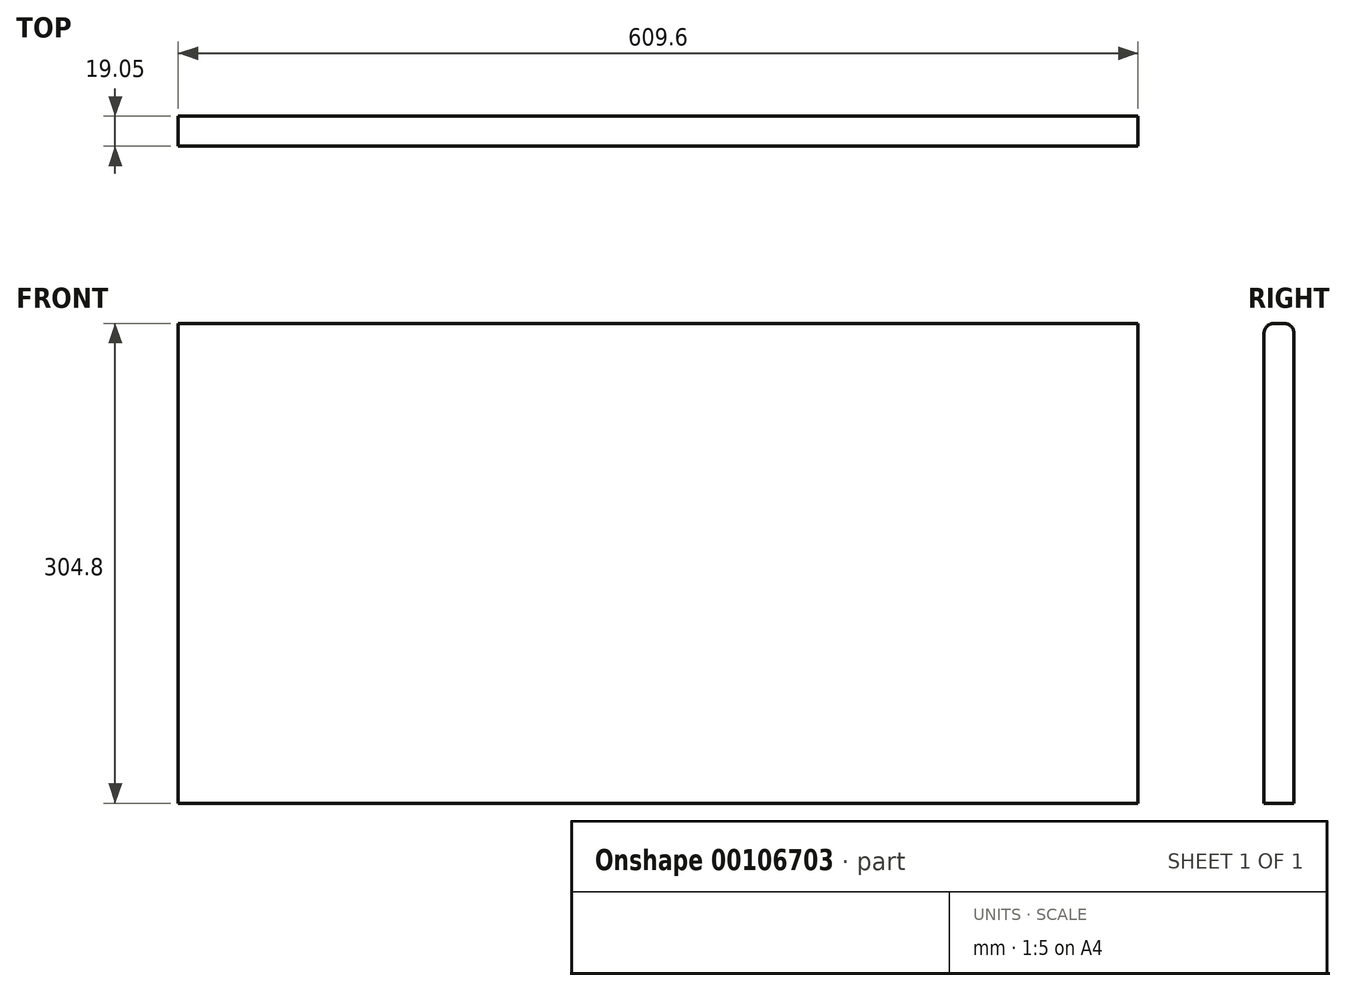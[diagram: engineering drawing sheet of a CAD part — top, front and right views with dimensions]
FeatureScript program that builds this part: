
annotation { "Feature Type Name" : "Feature", "Feature Type Description" : "" }
export const myFeature = defineFeature(function(context is Context, id is Id, definition is map)
    precondition{}
    {
        {
            var Q0;
            Q0=qCreatedBy(makeId("Front.planeOp"),FACE);
            var sketch = newSketch(context, id + "F0", { "sketchPlane" : qUnion([Q0])});
            skLineSegment(sketch, "E0.bottom", {"start": v(0, 0) * mm, "end": v(609.6, 0) * mm});
            skLineSegment(sketch, "E0.top", {"start": v(0, 304.8) * mm, "end": v(609.6, 304.8) * mm});
            skLineSegment(sketch, "E0.left", {"start": v(0, 0) * mm, "end": v(0, 304.8) * mm});
            skLineSegment(sketch, "E0.right", {"start": v(609.6, 0) * mm, "end": v(609.6, 304.8) * mm});
            skSolve(sketch);
        }
        {
            var Q0;
            Q0=makeQuery(id+"F0.imprint","IMPRINT",FACE,{"disambiguationData":[TD([[makeQuery(id+"F0.imprint","IMPRINT",EDGE,{"derivedFrom":sQuery(id+"F0.wireOp",EDGE,"E0.bottom")}),1.0]])]});
            extrude(context, id + "F1", {"entities" : qUnion([Q0]), "depth" : 19.05 * mm});
        }
        {
            var Q0;
            Q0=makeQuery(id+"F1.opExtrude","CAP_EDGE",EDGE,{"disambiguationData":[OSD([sQuery(id+"F0.wireOp",EDGE,"E0.top")])],"isStart":false});
            var Q1;
            Q1=makeQuery(id+"F1.opExtrude","CAP_EDGE",EDGE,{"disambiguationData":[OSD([sQuery(id+"F0.wireOp",EDGE,"E0.top")])],"isStart":true});
            fillet(context, id + "F2", {"entities" : qUnion([Q0, Q1]), "radius" : 6.35 * mm, "tangentPropagation" : true, "allowEdgeOverflow" : false});
        }
    });
